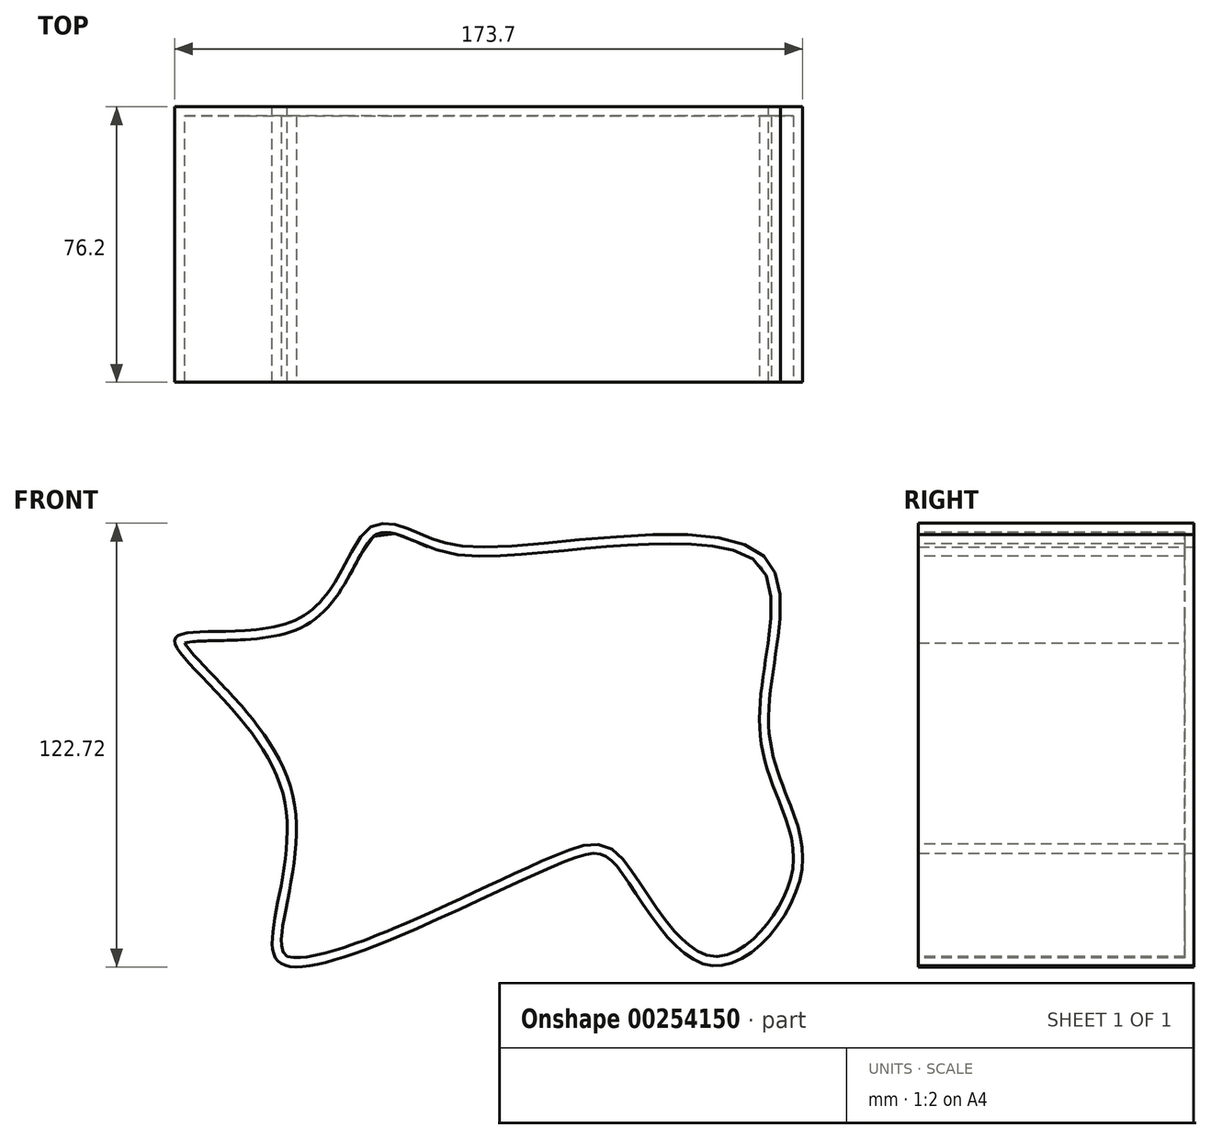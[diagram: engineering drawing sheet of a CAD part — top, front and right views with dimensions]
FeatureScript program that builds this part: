
annotation { "Feature Type Name" : "Feature", "Feature Type Description" : "" }
export const myFeature = defineFeature(function(context is Context, id is Id, definition is map)
    precondition{}
    {
        {
            var Q0;
            Q0=qCreatedBy(makeId("Front.planeOp"),FACE);
            var sketch = newSketch(context, id + "F0", { "sketchPlane" : qUnion([Q0])});
            skLineSegment(sketch, "E0.bottom", {"start": v(50.8, -50.8) * mm, "end": v(-50.8, -50.8) * mm});
            skLineSegment(sketch, "E0.top", {"start": v(50.8, 50.8) * mm, "end": v(-50.8, 50.8) * mm});
            skLineSegment(sketch, "E0.left", {"start": v(76.2, -25.4) * mm, "end": v(76.2, 25.4) * mm});
            skLineSegment(sketch, "E0.right", {"start": v(-76.2, -25.4) * mm, "end": v(-76.2, 25.4) * mm});
            skPoint(sketch, "E0.middle", {"position": v(0, 0) * mm});
            skPoint(sketch, "E1.visualSharp", {"position": v(-76.2, 50.8) * mm});
            skArc(sketch, "E1.filletArc", {"start": v(-50.8, 50.8) * mm, "mid": v(-68.76, 43.36) * mm, "end": v(-76.2, 25.4) * mm});
            skPoint(sketch, "E2.visualSharp", {"position": v(76.2, 50.8) * mm});
            skArc(sketch, "E2.filletArc", {"start": v(76.2, 25.4) * mm, "mid": v(68.76, 43.36) * mm, "end": v(50.8, 50.8) * mm});
            skPoint(sketch, "E3.visualSharp", {"position": v(76.2, -50.8) * mm});
            skArc(sketch, "E3.filletArc", {"start": v(50.8, -50.8) * mm, "mid": v(68.76, -43.36) * mm, "end": v(76.2, -25.4) * mm});
            skPoint(sketch, "E4.visualSharp", {"position": v(-76.2, -50.8) * mm});
            skArc(sketch, "E4.filletArc", {"start": v(-76.2, -25.4) * mm, "mid": v(-68.76, -43.36) * mm, "end": v(-50.8, -50.8) * mm});
            skPoint(sketch, "E5.11.internal.snap0", {"position": v(68.76, 43.36) * mm});
            skFitSpline(sketch, "E5", {"points": [v(-28.45, 61.79) * mm, v(-40.45, 62.23) * mm, v(-59.79, 37.34) * mm, v(-94.01, 31.78) * mm, v(-64.23, -10.9) * mm, v(-64.45, -58.23) * mm, v(15.11, -29.34) * mm, v(28.45, -31.56) * mm, v(54.23, -58.67) * mm, v(79.34, -32) * mm, v(70.23, 6.45) * mm, v(68.76, 54.67) * mm, v(-9.11, 57.12) * mm, v(-28.45, 61.79) * mm]});
            skSolve(sketch);
        }
        {
            var Q0;
            {var subQ13=sQuery(id+"F0.wireOp",EDGE,"E3.filletArc");Q0=makeQuery(id+"F0.imprint","IMPRINT",FACE,{"disambiguationData":[TD([[makeQuery(id+"F0.imprint","IMPRINT",EDGE,{"derivedFrom":subQ13}),1.0]])]});}
            var Q1;
            {var subQ0=sQuery(id+"F0.wireOp",EDGE,"E1.filletArc");var subQ1=sQuery(id+"F0.wireOp",EDGE,"E0.right");var subQ2=makeQuery(id+"F0.imprint","INTERSECT",VERTEX,{"derivedFrom":[subQ1,subQ0]});Q1=makeQuery(id+"F0.imprint","IMPRINT",FACE,{"disambiguationData":[TD([[makeQuery(id+"F0.imprint","IMPRINT",EDGE,{"disambiguationData":[TD([[subQ2,1.0]])],"derivedFrom":subQ1}),1.0]])]});}
            var Q2;
            {var subQ0=sQuery(id+"F0.wireOp",EDGE,"E2.filletArc");var subQ1=sQuery(id+"F0.wireOp",EDGE,"E0.top");var subQ2=makeQuery(id+"F0.imprint","INTERSECT",VERTEX,{"derivedFrom":[subQ1,subQ0]});Q2=makeQuery(id+"F0.imprint","IMPRINT",FACE,{"disambiguationData":[TD([[makeQuery(id+"F0.imprint","IMPRINT",EDGE,{"disambiguationData":[TD([[subQ2,-1.0]])],"derivedFrom":subQ1}),-1.0]])]});}
            var Q3;
            {var subQ0=sQuery(id+"F0.wireOp",EDGE,"E3.filletArc");Q3=makeQuery(id+"F0.imprint","IMPRINT",FACE,{"disambiguationData":[TD([[makeQuery(id+"F0.imprint","IMPRINT",EDGE,{"derivedFrom":subQ0}),-1.0]])]});}
            var Q4;
            {var subQ0=sQuery(id+"F0.wireOp",EDGE,"E4.filletArc");var subQ1=sQuery(id+"F0.wireOp",EDGE,"E0.bottom");var subQ2=makeQuery(id+"F0.imprint","INTERSECT",VERTEX,{"derivedFrom":[subQ1,subQ0]});Q4=makeQuery(id+"F0.imprint","IMPRINT",FACE,{"disambiguationData":[TD([[makeQuery(id+"F0.imprint","IMPRINT",EDGE,{"disambiguationData":[TD([[subQ2,1.0]])],"derivedFrom":subQ1}),1.0]])]});}
            extrude(context, id + "F1", {"entities" : qUnion([Q0, Q1, Q2, Q3, Q4]), "depth" : 76.2 * mm});
        }
        {
            var Q0;
            Q0=makeQuery(id+"F1.opExtrude","CAP_FACE",FACE,{"disambiguationData":[OSD([sQuery(id+"F0.wireOp",EDGE,"E5")])],"isStart":false});
            shell(context, id + "F2", {"entities" : qUnion([Q0]), "thickness" : 2.54 * mm});
        }
    });
